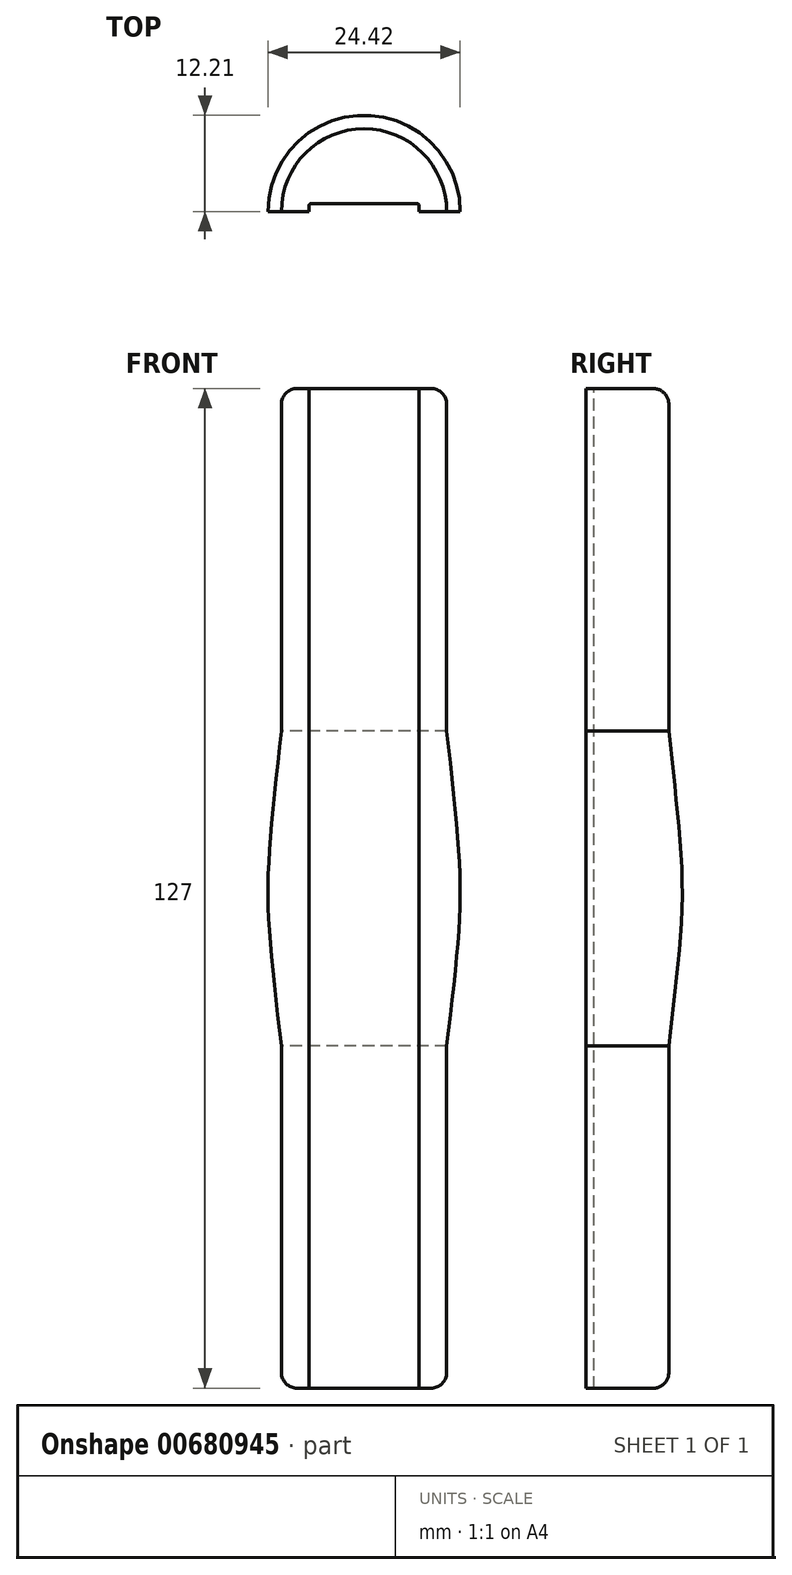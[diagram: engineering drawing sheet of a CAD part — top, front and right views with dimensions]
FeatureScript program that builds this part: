
annotation { "Feature Type Name" : "Feature", "Feature Type Description" : "" }
export const myFeature = defineFeature(function(context is Context, id is Id, definition is map)
    precondition{}
    {
        {
            var Q0;
            Q0=qCreatedBy(makeId("Front.planeOp"),FACE);
            var sketch = newSketch(context, id + "F0", { "sketchPlane" : qUnion([Q0])});
            skLineSegment(sketch, "E0.bottom", {"start": v(-5.25, 63.5) * mm, "end": v(5.25, 63.5) * mm});
            skLineSegment(sketch, "E0.top", {"start": v(-5.25, -63.5) * mm, "end": v(5.25, -63.5) * mm});
            skLineSegment(sketch, "E0.left", {"start": v(-5.25, 63.5) * mm, "end": v(-5.25, 20) * mm});
            skLineSegment(sketch, "E0.right", {"start": v(5.25, 63.5) * mm, "end": v(5.25, -63.5) * mm});
            skPoint(sketch, "E0.middle", {"position": v(0, 0) * mm});
            skFitSpline(sketch, "E1", {"points": [v(-5.25, 20) * mm, v(-6.8, 4.2) * mm, v(-6.8, -5.12) * mm, v(-5.25, -20) * mm], "startDerivative": vector(-5.22, -46.75) * mm, "endDerivative": vector(5.38, -45.13) * mm});
            skLineSegment(sketch, "E2.trimOffspring", {"start": v(-5.25, -20) * mm, "end": v(-5.25, -63.5) * mm});
            skPoint(sketch, "E3.orphan", {"position": v(-5.25, 0) * mm});
            skSolve(sketch);
        }
        {
            var Q0;
            Q0=makeQuery(id+"F0.imprint","IMPRINT",FACE,{"disambiguationData":[TD([[makeQuery(id+"F0.imprint","IMPRINT",EDGE,{"derivedFrom":sQuery(id+"F0.wireOp",EDGE,"E0.bottom")}),-1.0]])]});
            var Q1;
            Q1=sQuery(id+"F0.wireOp",EDGE,"E0.right");
            revolve(context, id + "F1", {"entities" : qUnion([Q0]), "axis" : qUnion([Q1]), "revolveType" : RevolveType.ONE_DIRECTION, "angle" : 180 * degree});
        }
        {
            var Q0;
            Q0=makeQuery(id+"F1.opRevolve","SWEPT_FACE",FACE,{"disambiguationData":[OSD([sQuery(id+"F0.wireOp",EDGE,"E0.bottom")])]});
            var sketch = newSketch(context, id + "F2", { "sketchPlane" : qUnion([Q0])});
            skLineSegment(sketch, "E4", {"start": v(5.25, 0) * mm, "end": v(-1.75, 0) * mm});
            skLineSegment(sketch, "E5", {"start": v(5.25, 0) * mm, "end": v(12.25, 0) * mm});
            skLineSegment(sketch, "E6", {"start": v(12.25, 0) * mm, "end": v(12.25, 0.7) * mm});
            skLineSegment(sketch, "E7", {"start": v(11.95, 1) * mm, "end": v(-1.45, 1) * mm});
            skLineSegment(sketch, "E8", {"start": v(-1.75, 0.7) * mm, "end": v(-1.75, 0) * mm});
            skPoint(sketch, "E9.visualSharp", {"position": v(-1.75, 1) * mm});
            skArc(sketch, "E9.filletArc", {"start": v(-1.45, 1) * mm, "mid": v(-1.66, 0.91) * mm, "end": v(-1.75, 0.7) * mm});
            skPoint(sketch, "E10.visualSharp", {"position": v(12.25, 1) * mm});
            skArc(sketch, "E10.filletArc", {"start": v(12.25, 0.7) * mm, "mid": v(12.16, 0.91) * mm, "end": v(11.95, 1) * mm});
            skSolve(sketch);
        }
        {
            var Q0;
            Q0=makeQuery(id+"F2.imprint","IMPRINT",FACE,{"disambiguationData":[TD([[makeQuery(id+"F2.imprint","IMPRINT",EDGE,{"derivedFrom":sQuery(id+"F2.wireOp",EDGE,"E4")}),-1.0]])]});
            extrude(context, id + "F3", {"entities" : qUnion([Q0]), "operationType" : NewBodyOperationType.REMOVE, "oppositeDirection" : true, "depth" : 127 * mm, "offsetDistance" : 25 * mm});
        }
        {
            var Q0;
            Q0=makeQuery(id+"F1.opRevolve","SWEPT_EDGE",EDGE,{"disambiguationData":[OSD([sQuery(id+"F0.wireOp",EDGE,"E0.bottom"),sQuery(id+"F0.wireOp",EDGE,"E0.left")])]});
            fillet(context, id + "F4", {"entities" : qUnion([Q0]), "radius" : 2 * mm, "tangentPropagation" : true, "allowEdgeOverflow" : false});
        }
        {
            var Q0;
            Q0=makeQuery(id+"F1.opRevolve","SWEPT_EDGE",EDGE,{"disambiguationData":[OSD([sQuery(id+"F0.wireOp",EDGE,"E0.top"),sQuery(id+"F0.wireOp",EDGE,"E2.trimOffspring")])]});
            fillet(context, id + "F5", {"entities" : qUnion([Q0]), "radius" : 2 * mm, "tangentPropagation" : true, "allowEdgeOverflow" : false});
        }
    });
